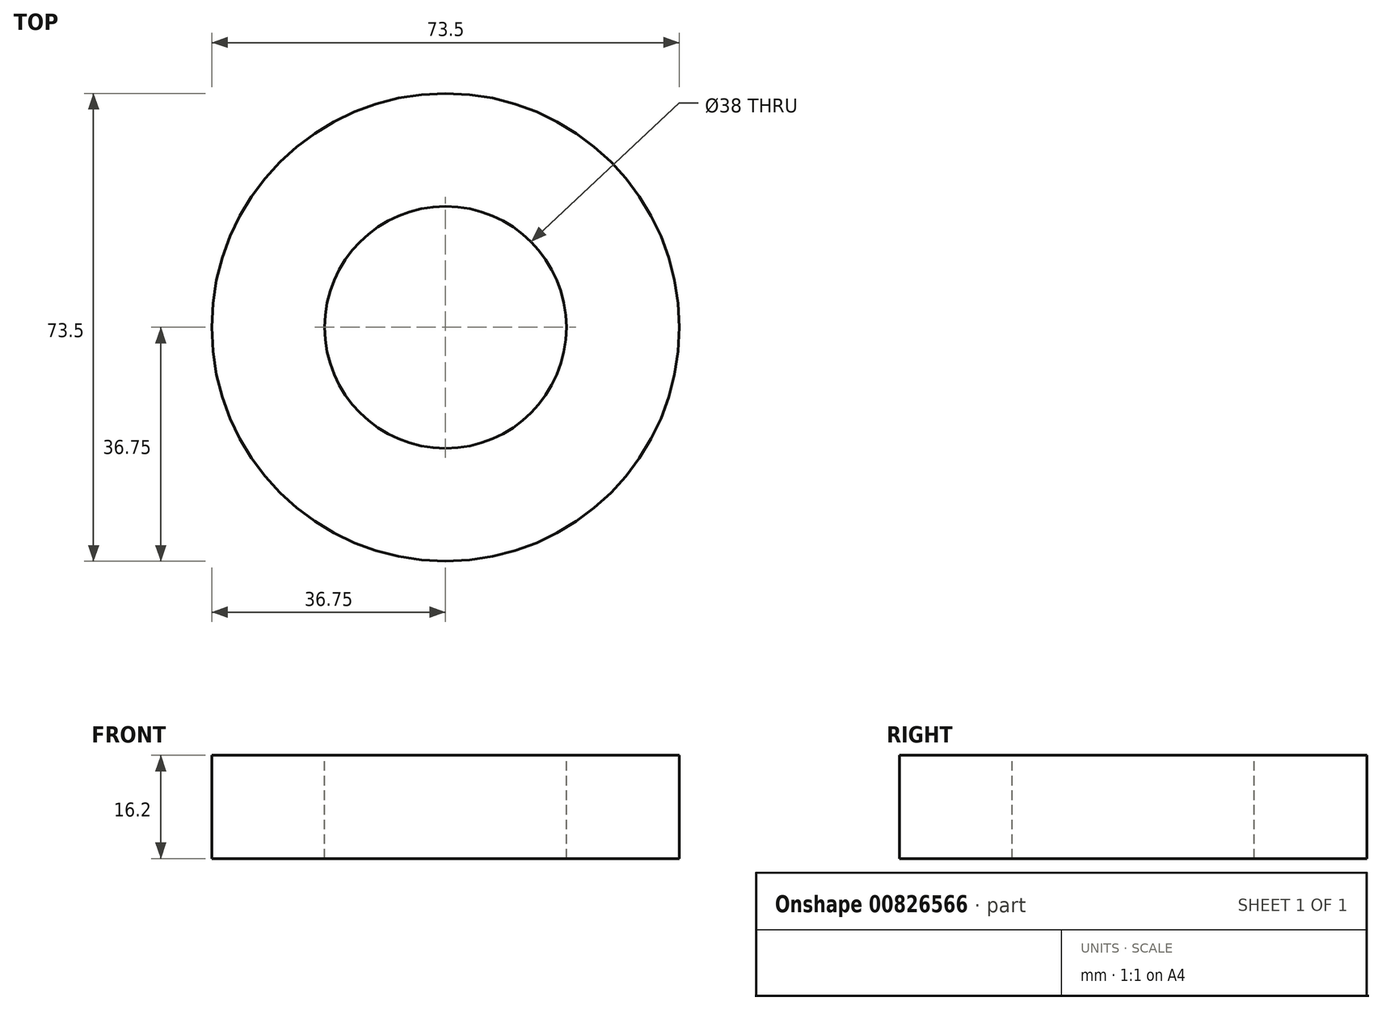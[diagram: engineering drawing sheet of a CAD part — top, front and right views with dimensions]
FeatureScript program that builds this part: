
annotation { "Feature Type Name" : "Feature", "Feature Type Description" : "" }
export const myFeature = defineFeature(function(context is Context, id is Id, definition is map)
    precondition{}
    {
        {
            var Q0;
            Q0=qCreatedBy(makeId("Front.planeOp"),FACE);
            var sketch = newSketch(context, id + "F0", { "sketchPlane" : qUnion([Q0])});
            skLineSegment(sketch, "E0.bottom", {"start": v(-36.75, 0) * mm, "end": v(-19, 0) * mm});
            skLineSegment(sketch, "E0.top", {"start": v(-36.75, 16.2) * mm, "end": v(-19, 16.2) * mm});
            skLineSegment(sketch, "E0.left", {"start": v(-36.75, 0) * mm, "end": v(-36.75, 16.2) * mm});
            skLineSegment(sketch, "E0.right", {"start": v(-19, 0) * mm, "end": v(-19, 16.2) * mm});
            skLineSegment(sketch, "E1", {"start": v(0, 40.68) * mm, "end": v(0, -37.83) * mm, "construction": true});
            skSolve(sketch);
        }
        {
            var Q0;
            Q0 = qSketchRegion(id + "F0", true);
            var Q1;
            Q1=sQuery(id+"F0.wireOp",EDGE,"E1");
            revolve(context, id + "F1", {"surfaceOperationType" : NewSurfaceOperationType.NEW, "entities" : qUnion([Q0]), "axis" : qUnion([Q1]), "revolveType" : RevolveType.FULL});
        }
    });
